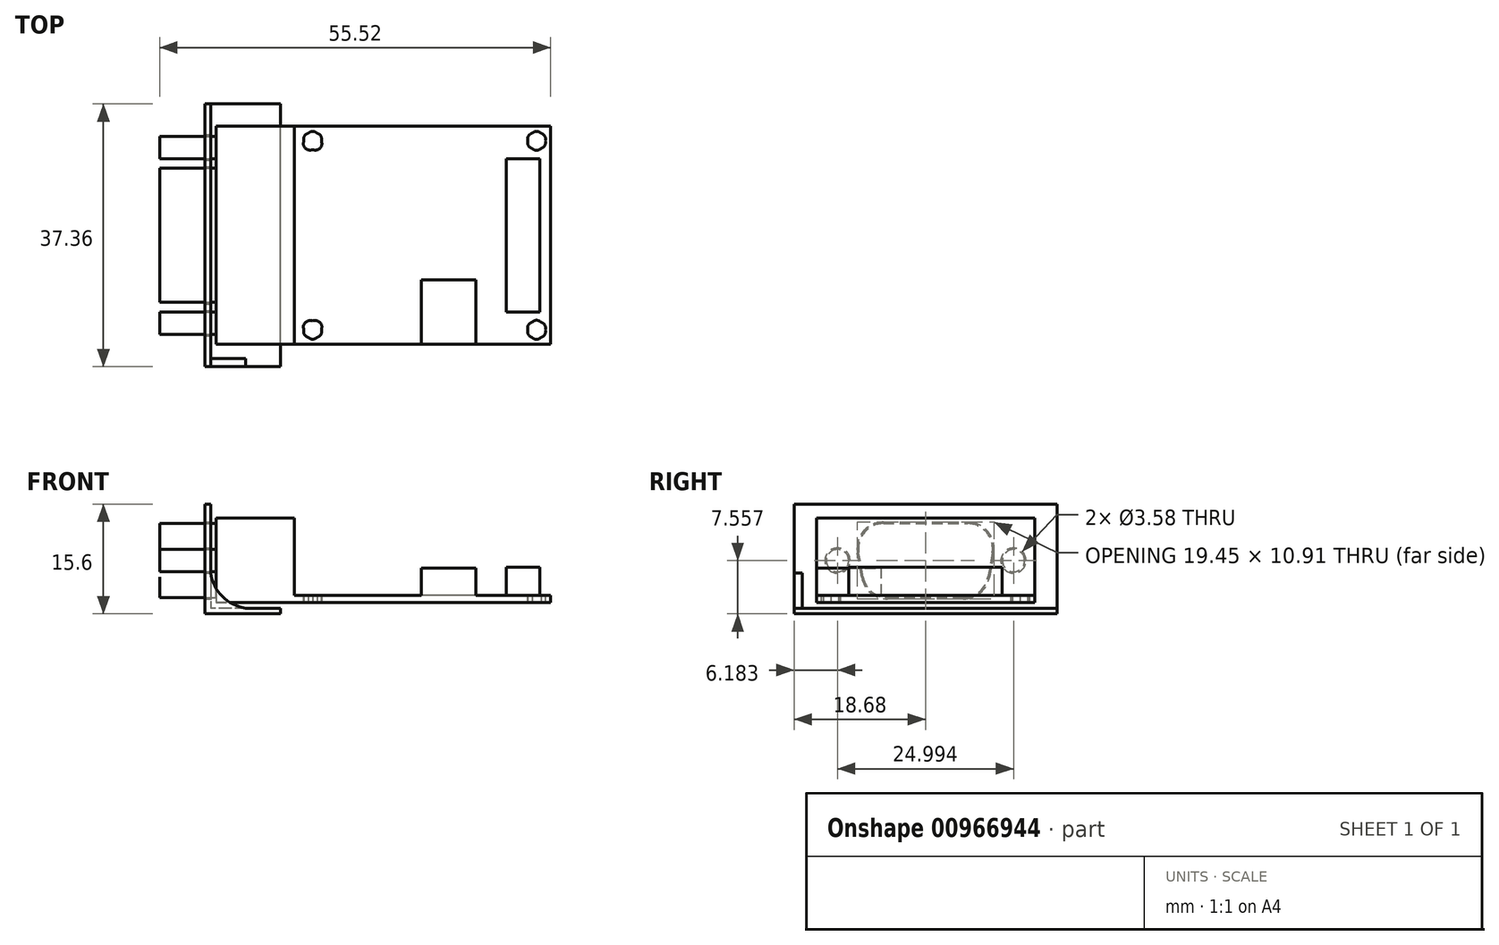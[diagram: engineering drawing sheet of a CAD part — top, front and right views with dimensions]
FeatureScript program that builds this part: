
annotation { "Feature Type Name" : "Feature", "Feature Type Description" : "" }
export const myFeature = defineFeature(function(context is Context, id is Id, definition is map)
    precondition{}
    {
        {
            var Q0;
            Q0=qCreatedBy(makeId("Top.planeOp"),FACE);
            var sketch = newSketch(context, id + "F0", { "sketchPlane" : qUnion([Q0])});
            skLineSegment(sketch, "E0", {"start": v(-23.76, -15.5) * mm, "end": v(23.76, -15.5) * mm});
            skLineSegment(sketch, "E1", {"start": v(23.76, -15.5) * mm, "end": v(23.76, 15.5) * mm});
            skLineSegment(sketch, "E2", {"start": v(23.76, 15.5) * mm, "end": v(-23.76, 15.5) * mm});
            skLineSegment(sketch, "E3", {"start": v(-23.76, 15.5) * mm, "end": v(-23.76, -15.5) * mm});
            skFitSpline(sketch, "E4", {"points": [v(-8.78, 13.42) * mm, v(-8.78, 12.72) * mm, v(-9.35, 12.16) * mm, v(-10.04, 12.16) * mm]});
            skFitSpline(sketch, "E5", {"points": [v(-10.04, 12.16) * mm, v(-10.74, 12.16) * mm, v(-11.3, 12.72) * mm, v(-11.3, 13.42) * mm]});
            skFitSpline(sketch, "E6", {"points": [v(-11.3, 13.42) * mm, v(-11.3, 13.87) * mm, v(-11.06, 14.28) * mm, v(-10.67, 14.5) * mm]});
            skFitSpline(sketch, "E7", {"points": [v(-10.67, 14.5) * mm, v(-10.28, 14.73) * mm, v(-9.8, 14.73) * mm, v(-9.41, 14.5) * mm]});
            skFitSpline(sketch, "E8", {"points": [v(-9.41, 14.5) * mm, v(-9.02, 14.28) * mm, v(-8.78, 13.87) * mm, v(-8.78, 13.42) * mm]});
            skFitSpline(sketch, "E9", {"points": [v(23.02, 13.42) * mm, v(23.02, 12.97) * mm, v(22.77, 12.56) * mm, v(22.38, 12.33) * mm]});
            skFitSpline(sketch, "E10", {"points": [v(22.38, 12.33) * mm, v(22, 12.1) * mm, v(21.51, 12.1) * mm, v(21.12, 12.33) * mm]});
            skFitSpline(sketch, "E11", {"points": [v(21.12, 12.33) * mm, v(20.73, 12.56) * mm, v(20.5, 12.97) * mm, v(20.5, 13.42) * mm]});
            skFitSpline(sketch, "E12", {"points": [v(20.5, 13.42) * mm, v(20.5, 13.87) * mm, v(20.73, 14.3) * mm, v(21.12, 14.52) * mm]});
            skFitSpline(sketch, "E13", {"points": [v(21.12, 14.52) * mm, v(21.51, 14.74) * mm, v(22, 14.74) * mm, v(22.38, 14.52) * mm]});
            skFitSpline(sketch, "E14", {"points": [v(22.38, 14.52) * mm, v(22.77, 14.3) * mm, v(23.02, 13.87) * mm, v(23.02, 13.42) * mm]});
            skFitSpline(sketch, "E15", {"points": [v(-13.94, 11.79) * mm, v(-13.94, 11.3) * mm, v(-14.2, 10.85) * mm, v(-14.63, 10.6) * mm]});
            skFitSpline(sketch, "E16", {"points": [v(-14.63, 10.6) * mm, v(-15.06, 10.35) * mm, v(-15.58, 10.35) * mm, v(-16, 10.6) * mm]});
            skFitSpline(sketch, "E17", {"points": [v(-16, 10.6) * mm, v(-16.43, 10.85) * mm, v(-16.7, 11.3) * mm, v(-16.7, 11.79) * mm]});
            skFitSpline(sketch, "E18", {"points": [v(-16.7, 11.79) * mm, v(-16.7, 12.28) * mm, v(-16.43, 12.73) * mm, v(-16, 12.98) * mm]});
            skFitSpline(sketch, "E19", {"points": [v(-16, 12.98) * mm, v(-15.58, 13.22) * mm, v(-15.06, 13.22) * mm, v(-14.63, 12.98) * mm]});
            skFitSpline(sketch, "E20", {"points": [v(-14.63, 12.98) * mm, v(-14.2, 12.73) * mm, v(-13.94, 12.28) * mm, v(-13.94, 11.79) * mm]});
            skFitSpline(sketch, "E21", {"points": [v(-8.78, -13.42) * mm, v(-8.78, -12.72) * mm, v(-9.35, -12.16) * mm, v(-10.04, -12.16) * mm]});
            skFitSpline(sketch, "E22", {"points": [v(-10.04, -12.16) * mm, v(-10.74, -12.16) * mm, v(-11.3, -12.72) * mm, v(-11.3, -13.42) * mm]});
            skFitSpline(sketch, "E23", {"points": [v(-11.3, -13.42) * mm, v(-11.3, -13.87) * mm, v(-11.06, -14.28) * mm, v(-10.67, -14.5) * mm]});
            skFitSpline(sketch, "E24", {"points": [v(-10.67, -14.5) * mm, v(-10.28, -14.73) * mm, v(-9.8, -14.73) * mm, v(-9.41, -14.5) * mm]});
            skFitSpline(sketch, "E25", {"points": [v(-9.41, -14.5) * mm, v(-9.02, -14.28) * mm, v(-8.78, -13.87) * mm, v(-8.78, -13.42) * mm]});
            skFitSpline(sketch, "E26", {"points": [v(23.02, -13.42) * mm, v(23.02, -12.97) * mm, v(22.77, -12.56) * mm, v(22.38, -12.33) * mm]});
            skFitSpline(sketch, "E27", {"points": [v(22.38, -12.33) * mm, v(22, -12.1) * mm, v(21.51, -12.1) * mm, v(21.12, -12.33) * mm]});
            skFitSpline(sketch, "E28", {"points": [v(21.12, -12.33) * mm, v(20.73, -12.56) * mm, v(20.5, -12.97) * mm, v(20.5, -13.42) * mm]});
            skFitSpline(sketch, "E29", {"points": [v(20.5, -13.42) * mm, v(20.5, -13.87) * mm, v(20.73, -14.3) * mm, v(21.12, -14.52) * mm]});
            skFitSpline(sketch, "E30", {"points": [v(21.12, -14.52) * mm, v(21.51, -14.74) * mm, v(22, -14.74) * mm, v(22.38, -14.52) * mm]});
            skFitSpline(sketch, "E31", {"points": [v(22.38, -14.52) * mm, v(22.77, -14.3) * mm, v(23.02, -13.87) * mm, v(23.02, -13.42) * mm]});
            skFitSpline(sketch, "E32", {"points": [v(-13.94, -11.79) * mm, v(-13.94, -11.3) * mm, v(-14.2, -10.85) * mm, v(-14.63, -10.6) * mm]});
            skFitSpline(sketch, "E33", {"points": [v(-14.63, -10.6) * mm, v(-15.06, -10.35) * mm, v(-15.58, -10.35) * mm, v(-16, -10.6) * mm]});
            skFitSpline(sketch, "E34", {"points": [v(-16, -10.6) * mm, v(-16.43, -10.85) * mm, v(-16.7, -11.3) * mm, v(-16.7, -11.79) * mm]});
            skFitSpline(sketch, "E35", {"points": [v(-16.7, -11.79) * mm, v(-16.7, -12.28) * mm, v(-16.43, -12.73) * mm, v(-16, -12.98) * mm]});
            skFitSpline(sketch, "E36", {"points": [v(-16, -12.98) * mm, v(-15.58, -13.22) * mm, v(-15.06, -13.22) * mm, v(-14.63, -12.98) * mm]});
            skFitSpline(sketch, "E37", {"points": [v(-14.63, -12.98) * mm, v(-14.2, -12.73) * mm, v(-13.94, -12.28) * mm, v(-13.94, -11.79) * mm]});
            skSolve(sketch);
        }
        {
            var Q0;
            Q0=makeQuery(id+"F0.imprint","IMPRINT",FACE,{"disambiguationData":[TD([[makeQuery(id+"F0.imprint","IMPRINT",EDGE,{"derivedFrom":sQuery(id+"F0.wireOp",EDGE,"E0")}),1.0]])]});
            extrude(context, id + "F1", {"entities" : qUnion([Q0]), "depth" : 1 * mm, "offsetDistance" : 25 * mm});
        }
        {
            var Q0;
            Q0=qCreatedBy(makeId("Top.planeOp"),FACE);
            var sketch = newSketch(context, id + "F2", { "sketchPlane" : qUnion([Q0])});
            skLineSegment(sketch, "E38.bottom", {"start": v(17.43, 10.9) * mm, "end": v(22.23, 10.9) * mm});
            skLineSegment(sketch, "E38.top", {"start": v(17.43, -10.9) * mm, "end": v(22.23, -10.9) * mm});
            skLineSegment(sketch, "E38.left", {"start": v(17.43, 10.9) * mm, "end": v(17.43, -10.9) * mm});
            skLineSegment(sketch, "E38.right", {"start": v(22.23, 10.9) * mm, "end": v(22.23, -10.9) * mm});
            skSolve(sketch);
        }
        {
            var Q0;
            Q0 = qSketchRegion(id + "F2", true);
            extrude(context, id + "F3", {"entities" : qUnion([Q0]), "operationType" : NewBodyOperationType.ADD, "depth" : 5 * mm, "offsetDistance" : 25 * mm});
        }
        {
            var Q0;
            Q0=qCreatedBy(makeId("Top.planeOp"),FACE);
            var sketch = newSketch(context, id + "F4", { "sketchPlane" : qUnion([Q0])});
            skLineSegment(sketch, "E39.bottom", {"start": v(-23.76, 15.5) * mm, "end": v(-12.66, 15.5) * mm});
            skLineSegment(sketch, "E39.top", {"start": v(-23.76, -15.5) * mm, "end": v(-12.66, -15.5) * mm});
            skLineSegment(sketch, "E39.left", {"start": v(-23.76, 15.5) * mm, "end": v(-23.76, -15.5) * mm});
            skLineSegment(sketch, "E39.right", {"start": v(-12.66, 15.5) * mm, "end": v(-12.66, -15.5) * mm});
            skSolve(sketch);
        }
        {
            var Q0;
            Q0 = qSketchRegion(id + "F4", true);
            extrude(context, id + "F5", {"entities" : qUnion([Q0]), "operationType" : NewBodyOperationType.ADD, "depth" : 12 * mm, "offsetDistance" : 25 * mm});
        }
        {
            var Q0;
            Q0=makeQuery(id+"F5.boolean.opBoolean","MERGE",FACE,{"derivedFrom":[makeQuery(id+"F1.opExtrude","SWEPT_FACE",FACE,{"disambiguationData":[OSD([sQuery(id+"F0.wireOp",EDGE,"E3")])]}),makeQuery(id+"F5.opExtrude","SWEPT_FACE",FACE,{"disambiguationData":[OSD([sQuery(id+"F4.wireOp",EDGE,"E39.left")])]})]});
            cPlane(context, id + "F6", {"entities" : qUnion([Q0]), "cplaneType" : CPlaneType.OFFSET, "offset" : 0 * mm, "width" : 150 * mm, "height" : 150 * mm});
        }
        {
            var Q0;
            Q0=qCreatedBy(id+"F6.planeOp",FACE);
            var sketch = newSketch(context, id + "F7", { "sketchPlane" : qUnion([Q0])});
            skCircle(sketch, "E40", {"center": v(-12.5, 5.96) * mm, "radius": 1.59 * mm});
            skArc(sketch, "E41", {"start": v(9.48, 7.05) * mm, "mid": v(8.7, 9.95) * mm, "end": v(5.98, 11.21) * mm});
            skLineSegment(sketch, "E42", {"start": v(5.98, 11.21) * mm, "end": v(-5.98, 11.21) * mm});
            skArc(sketch, "E43", {"start": v(-5.98, 11.21) * mm, "mid": v(-8.7, 9.95) * mm, "end": v(-9.48, 7.05) * mm});
            skLineSegment(sketch, "E44", {"start": v(-9.48, 7.05) * mm, "end": v(-8.87, 3.63) * mm});
            skArc(sketch, "E45", {"start": v(-8.87, 3.63) * mm, "mid": v(-7.66, 1.53) * mm, "end": v(-5.38, 0.7) * mm});
            skLineSegment(sketch, "E46", {"start": v(-5.38, 0.7) * mm, "end": v(5.38, 0.7) * mm});
            skArc(sketch, "E47", {"start": v(5.38, 0.7) * mm, "mid": v(7.66, 1.53) * mm, "end": v(8.87, 3.63) * mm});
            skLineSegment(sketch, "E48", {"start": v(8.87, 3.63) * mm, "end": v(9.48, 7.05) * mm});
            skCircle(sketch, "E49", {"center": v(12.5, 5.96) * mm, "radius": 1.59 * mm});
            skSolve(sketch);
        }
        {
            var Q0;
            Q0 = qSketchRegion(id + "F7", true);
            extrude(context, id + "F8", {"entities" : qUnion([Q0]), "operationType" : NewBodyOperationType.ADD, "depth" : 8 * mm, "offsetDistance" : 25 * mm});
        }
        {
            var Q0;
            Q0=qCreatedBy(makeId("Top.planeOp"),FACE);
            var sketch = newSketch(context, id + "F9", { "sketchPlane" : qUnion([Q0])});
            skLineSegment(sketch, "E50.bottom", {"start": v(5.41, -15.5) * mm, "end": v(13.11, -15.5) * mm});
            skLineSegment(sketch, "E50.top", {"start": v(5.41, -6.3) * mm, "end": v(13.11, -6.3) * mm});
            skLineSegment(sketch, "E50.left", {"start": v(5.41, -15.5) * mm, "end": v(5.41, -6.3) * mm});
            skLineSegment(sketch, "E50.right", {"start": v(13.11, -15.5) * mm, "end": v(13.11, -6.3) * mm});
            skSolve(sketch);
        }
        {
            var Q0;
            Q0 = qSketchRegion(id + "F9", true);
            extrude(context, id + "F10", {"entities" : qUnion([Q0]), "operationType" : NewBodyOperationType.ADD, "depth" : 4.9 * mm, "offsetDistance" : 25 * mm});
        }
        {
            var Q0;
            Q0=qCreatedBy(makeId("Top.planeOp"),FACE);
            var sketch = newSketch(context, id + "F11", { "sketchPlane" : qUnion([Q0])});
            skLineSegment(sketch, "E51.0", {"start": v(29.67, 18.68) * mm, "end": v(29.67, -18.68) * mm});
            skLineSegment(sketch, "E51.1", {"start": v(29.67, 18.68) * mm, "end": v(-25.33, 18.68) * mm});
            skLineSegment(sketch, "E51.2", {"start": v(-25.33, 18.68) * mm, "end": v(-25.33, -18.68) * mm});
            skLineSegment(sketch, "E51.3", {"start": v(29.67, -18.68) * mm, "end": v(-25.33, -18.68) * mm});
            skSolve(sketch);
        }
        {
            var Q0;
            Q0=makeQuery(id+"F11.imprint","IMPRINT",FACE,{"disambiguationData":[TD([[makeQuery(id+"F11.imprint","IMPRINT",EDGE,{"derivedFrom":sQuery(id+"F11.wireOp",EDGE,"E51.0")}),-1.0]])]});
            extrude(context, id + "F12", {"entities" : qUnion([Q0]), "depth" : 14 * mm, "offsetDistance" : 25 * mm, "hasSecondDirection" : true, "secondDirectionOppositeDirection" : true, "secondDirectionDepth" : 1.6 * mm});
        }
        {
            var Q0;
            Q0=makeQuery(id+"F12.opExtrude","CAP_FACE",FACE,{"disambiguationData":[OSD([sQuery(id+"F11.wireOp",EDGE,"E51.0"),sQuery(id+"F11.wireOp",EDGE,"E51.1"),sQuery(id+"F11.wireOp",EDGE,"E51.2"),sQuery(id+"F11.wireOp",EDGE,"E51.3")])],"isStart":false});
            var Q1;
            Q1=makeQuery(id+"F12.opExtrude","SWEPT_FACE",FACE,{"disambiguationData":[OSD([sQuery(id+"F11.wireOp",EDGE,"E51.0")])]});
            var Q2;
            Q2=makeQuery(id+"F12.opExtrude","SWEPT_FACE",FACE,{"disambiguationData":[OSD([sQuery(id+"F11.wireOp",EDGE,"E51.3")])]});
            var Q3;
            Q3=makeQuery(id+"F12.opExtrude","SWEPT_FACE",FACE,{"disambiguationData":[OSD([sQuery(id+"F11.wireOp",EDGE,"E51.1")])]});
            shell(context, id + "F13", {"entities" : qUnion([Q0, Q1, Q2, Q3]), "thickness" : 0.8 * mm});
        }
        {
            var Q0;
            Q0=makeQuery(id+"F1.opExtrude","SWEPT_BODY",BODY,{"disambiguationData":[OSD([sQuery(id+"F0.wireOp",EDGE,"E0"),sQuery(id+"F0.wireOp",EDGE,"E1"),sQuery(id+"F0.wireOp",EDGE,"E2"),sQuery(id+"F0.wireOp",EDGE,"E3"),sQuery(id+"F0.wireOp",EDGE,"E4"),sQuery(id+"F0.wireOp",EDGE,"E5"),sQuery(id+"F0.wireOp",EDGE,"E6"),sQuery(id+"F0.wireOp",EDGE,"E7"),sQuery(id+"F0.wireOp",EDGE,"E8"),sQuery(id+"F0.wireOp",EDGE,"E9"),sQuery(id+"F0.wireOp",EDGE,"E10"),sQuery(id+"F0.wireOp",EDGE,"E11"),sQuery(id+"F0.wireOp",EDGE,"E12"),sQuery(id+"F0.wireOp",EDGE,"E13"),sQuery(id+"F0.wireOp",EDGE,"E14"),sQuery(id+"F0.wireOp",EDGE,"E15"),sQuery(id+"F0.wireOp",EDGE,"E16"),sQuery(id+"F0.wireOp",EDGE,"E17"),sQuery(id+"F0.wireOp",EDGE,"E18"),sQuery(id+"F0.wireOp",EDGE,"E19"),sQuery(id+"F0.wireOp",EDGE,"E20"),sQuery(id+"F0.wireOp",EDGE,"E21"),sQuery(id+"F0.wireOp",EDGE,"E22"),sQuery(id+"F0.wireOp",EDGE,"E23"),sQuery(id+"F0.wireOp",EDGE,"E24"),sQuery(id+"F0.wireOp",EDGE,"E25"),sQuery(id+"F0.wireOp",EDGE,"E26"),sQuery(id+"F0.wireOp",EDGE,"E27"),sQuery(id+"F0.wireOp",EDGE,"E28"),sQuery(id+"F0.wireOp",EDGE,"E29"),sQuery(id+"F0.wireOp",EDGE,"E30"),sQuery(id+"F0.wireOp",EDGE,"E31"),sQuery(id+"F0.wireOp",EDGE,"E32"),sQuery(id+"F0.wireOp",EDGE,"E33"),sQuery(id+"F0.wireOp",EDGE,"E34"),sQuery(id+"F0.wireOp",EDGE,"E35"),sQuery(id+"F0.wireOp",EDGE,"E36"),sQuery(id+"F0.wireOp",EDGE,"E37")])]});
            var Q1;
            Q1=makeQuery(id+"F12.opExtrude","SWEPT_BODY",BODY,{"disambiguationData":[OSD([sQuery(id+"F11.wireOp",EDGE,"E51.0"),sQuery(id+"F11.wireOp",EDGE,"E51.1"),sQuery(id+"F11.wireOp",EDGE,"E51.2"),sQuery(id+"F11.wireOp",EDGE,"E51.3")])]});
            booleanBodies(context, id + "F14", {"operationType" : BooleanOperationType.SUBTRACTION, "tools" : qUnion([Q0]), "targets" : qUnion([Q1]), "offset" : true, "offsetAll" : true, "offsetDistance" : 0.2 * mm, "keepTools" : true});
        }
        {
            var Q0;
            Q0=qCreatedBy(makeId("Top.planeOp"),FACE);
            var sketch = newSketch(context, id + "F15", { "sketchPlane" : qUnion([Q0])});
            skLineSegment(sketch, "E52.bottom", {"start": v(-14.64, -24.48) * mm, "end": v(34.06, -24.48) * mm});
            skLineSegment(sketch, "E52.top", {"start": v(-14.64, 26.81) * mm, "end": v(34.06, 26.81) * mm});
            skLineSegment(sketch, "E52.left", {"start": v(-14.64, -24.48) * mm, "end": v(-14.64, 26.81) * mm});
            skLineSegment(sketch, "E52.right", {"start": v(34.06, -24.48) * mm, "end": v(34.06, 26.81) * mm});
            skSolve(sketch);
        }
        {
            var Q0;
            Q0 = qSketchRegion(id + "F15", true);
            extrude(context, id + "F16", {"entities" : qUnion([Q0]), "operationType" : NewBodyOperationType.REMOVE, "oppositeDirection" : true, "depth" : 25 * mm, "offsetDistance" : 25 * mm});
        }
        {
            var Q0;
            Q0=makeQuery(id+"F12.opExtrude","SWEPT_FACE",FACE,{"disambiguationData":[OSD([sQuery(id+"F11.wireOp",EDGE,"E51.3")])]});
            var sketch = newSketch(context, id + "F17", { "sketchPlane" : qUnion([Q0])});
            skArc(sketch, "E53", {"start": v(-24.53, 4.2) * mm, "mid": v(-22.88, 0.89) * mm, "end": v(-19.58, -0.8) * mm});
            skPoint(sketch, "E53.first.point", {"position": v(-24.53, 4.2) * mm});
            skPoint(sketch, "E53.second.point", {"position": v(-19.58, -0.8) * mm});
            skPoint(sketch, "E53.third.point", {"position": v(-14.68, 0.65) * mm});
            skLineSegment(sketch, "E54", {"start": v(-24.53, 4.2) * mm, "end": v(-24.53, -0.8) * mm});
            skLineSegment(sketch, "E55", {"start": v(-24.53, -0.8) * mm, "end": v(-19.58, -0.8) * mm});
            skSolve(sketch);
        }
        {
            var Q0;
            Q0 = qSketchRegion(id + "F17", true);
            extrude(context, id + "F18", {"entities" : qUnion([Q0]), "operationType" : NewBodyOperationType.ADD, "oppositeDirection" : true, "depth" : 1.2 * mm, "offsetDistance" : 25 * mm});
        }
    });
